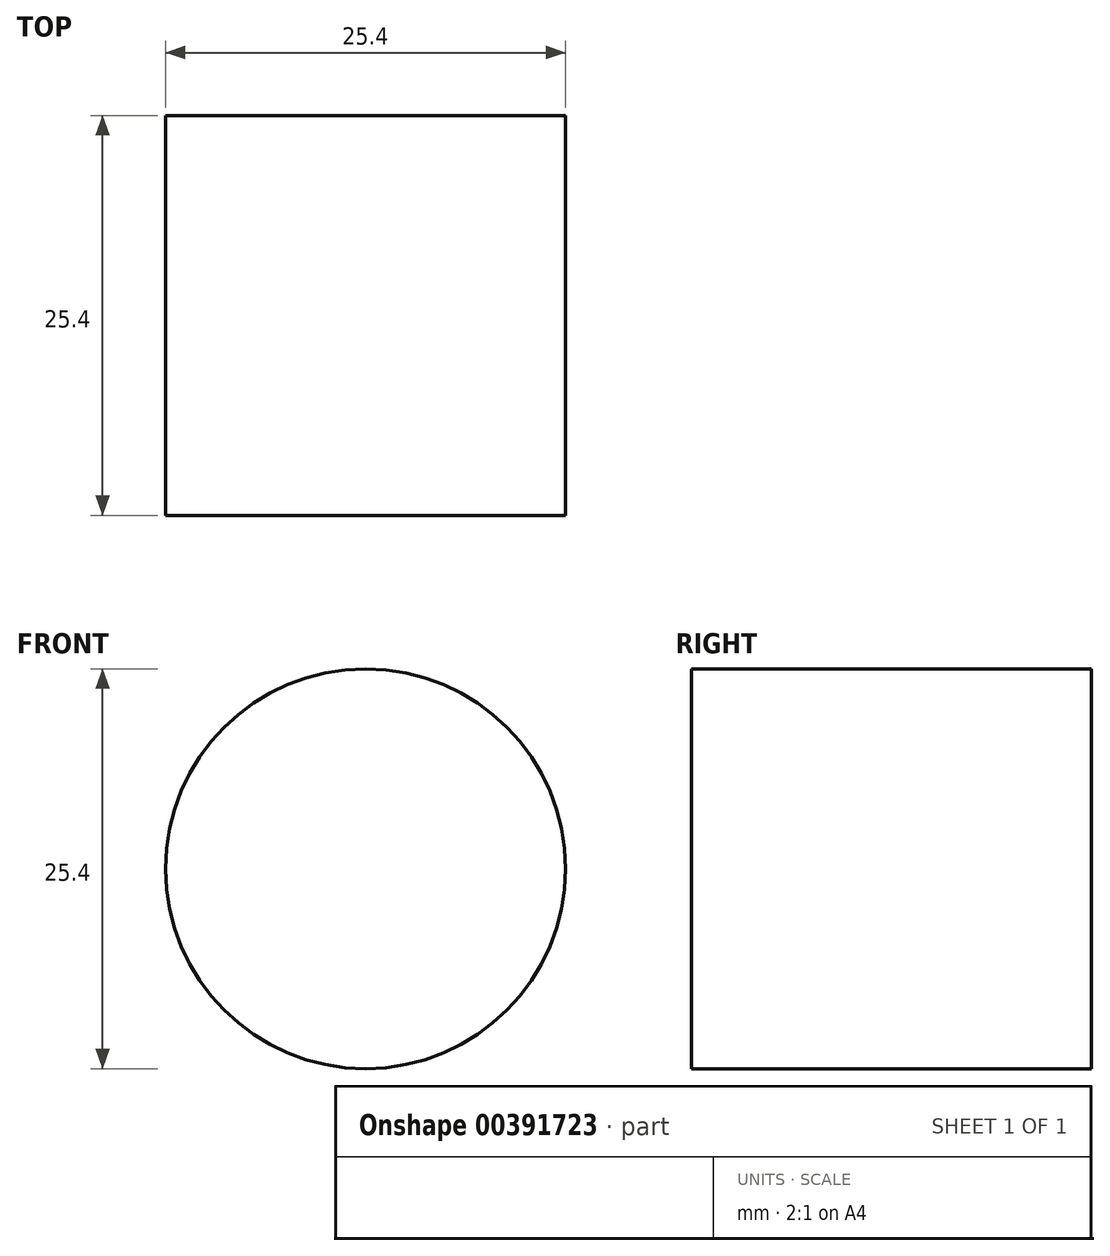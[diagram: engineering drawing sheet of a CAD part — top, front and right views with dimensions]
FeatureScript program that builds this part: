
annotation { "Feature Type Name" : "Feature", "Feature Type Description" : "" }
export const myFeature = defineFeature(function(context is Context, id is Id, definition is map)
    precondition{}
    {
        {
            var Q0;
            Q0=qCreatedBy(makeId("Top.planeOp"),FACE);
            var sketch = newSketch(context, id + "F0", { "sketchPlane" : qUnion([Q0])});
            skLineSegment(sketch, "E0.bottom", {"start": v(0, 0) * mm, "end": v(-12.7, 0) * mm});
            skLineSegment(sketch, "E0.left", {"start": v(0, 0) * mm, "end": v(0, 25.4) * mm});
            skLineSegment(sketch, "E1", {"start": v(0, 25.4) * mm, "end": v(-12.7, 25.4) * mm});
            skLineSegment(sketch, "E2", {"start": v(-12.7, 25.4) * mm, "end": v(-12.7, 0) * mm});
            skSolve(sketch);
        }
        {
            var Q0;
            Q0=makeQuery(id+"F0.imprint","IMPRINT",FACE,{"disambiguationData":[TD([[makeQuery(id+"F0.imprint","IMPRINT",EDGE,{"derivedFrom":sQuery(id+"F0.wireOp",EDGE,"E0.bottom")}),-1.0]])]});
            var Q1;
            Q1=sQuery(id+"F0.wireOp",EDGE,"E0.left");
            revolve(context, id + "F1", {"entities" : qUnion([Q0]), "axis" : qUnion([Q1]), "revolveType" : RevolveType.FULL});
        }
    });
